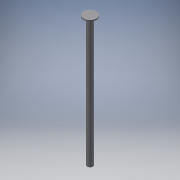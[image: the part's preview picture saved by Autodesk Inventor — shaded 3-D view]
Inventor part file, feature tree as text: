
AUTODESK INVENTOR PART (.ipt)
format: ipt  version: 2016 (Build 200138000, 138)  size: 92,160 bytes
history: native  units: in
note: dims shown in document units (in); Inventor stores cm internally (conversion verified against a paired STEP export)
features: extrude x2, sketch x2
ambient origin geometry x8: Origin, YZ Plane, XZ Plane, XY Plane, X Axis, Y Axis, Z Axis, Center Point
bodies: Solid1 (feature_tree)
feature tree (4):
  extrude  "Extrusion1"  Depth=3.4173in TaperAngle=0.0deg
  extrude  "Extrusion2"  Depth=0.0335in TaperAngle=0.0deg
  sketch  "Sketch1"  dims[d0=0.1496in d1=3.4173in d2=0.0in]
  sketch  "Sketch2"  dims[d3=0.3386in d4=0.0335in d5=0.0in]
